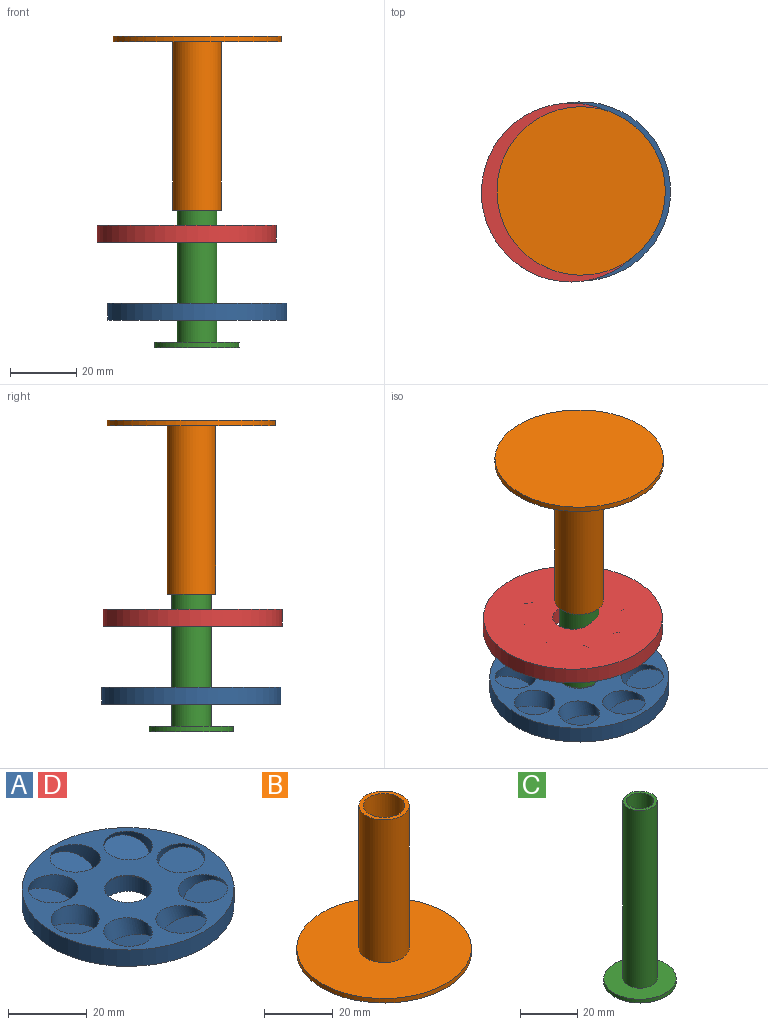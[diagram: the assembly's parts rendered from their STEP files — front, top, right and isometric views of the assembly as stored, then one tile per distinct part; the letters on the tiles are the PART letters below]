
ASSEMBLY  parts=4 mates=2
PART A: 22 faces, bbox 54.9x54.9x9.7 mm
  f0: cylinder r=26.99mm len=53.98mm, axis (0,0,-1), area 861.4mm2, adj f1,f2
  f1: plane 54.89x54.89mm, normal (0,0,1), area 1194.7mm2, adj f0,f4,f6,f8,f9,f11,f13,f15
  f2: plane 53.98x53.98mm, normal (0,0,-1), area 2171.4mm2, adj f0,f19
  f3: plane 12.02x11.79mm, normal (-0.17,0.25,0.95), area 116.7mm2, adj f4
  f4: cylinder r=6.1mm len=13.09mm, axis (-0.17,0.25,0.95), area 121.6mm2, adj f1,f3
  f5: plane 12.02x11.79mm, normal (0.17,-0.25,0.95), area 116.7mm2, adj f6
  f6: cylinder r=6.1mm len=13.09mm, axis (0.17,-0.25,0.95), area 121.4mm2, adj f1,f5
  f7: plane 12.02x11.79mm, normal (-0.25,-0.17,0.95), area 116.7mm2, adj f8
  f8: cylinder r=6.1mm len=13.09mm, axis (-0.25,-0.17,0.95), area 121.6mm2, adj f1,f7
  f9: cylinder r=6.1mm len=13.09mm, axis (0.25,0.17,0.95), area 121.4mm2, adj f1,f10
  f10: plane 12.02x11.79mm, normal (0.25,0.17,0.95), area 116.7mm2, adj f9
  f11: cylinder r=6.1mm len=13.17mm, axis (0.3,-0.06,0.95), area 121.6mm2, adj f1,f12
  f12: plane 12.17x11.64mm, normal (0.3,-0.06,0.95), area 116.7mm2, adj f11
  f13: cylinder r=6.1mm len=13.17mm, axis (-0.3,0.06,0.95), area 119.7mm2, adj f1,f14
  f14: plane 12.17x11.64mm, normal (-0.3,0.06,0.95), area 116.7mm2, adj f13
  f15: cylinder r=6.1mm len=13.17mm, axis (-0.06,-0.3,0.95), area 121.6mm2, adj f1,f16
  f16: plane 12.17x11.64mm, normal (-0.06,-0.3,0.95), area 116.7mm2, adj f15
  f17: cylinder r=6.1mm len=13.17mm, axis (0.06,0.3,0.95), area 119.7mm2, adj f1,f18
  f18: plane 12.17x11.64mm, normal (0.06,0.3,0.95), area 116.7mm2, adj f17
  f19: cylinder r=6.1mm len=12.19mm, axis (0,0,1), area 186.8mm2, adj f2,f20
  f20: plane 12.19x12.19mm, normal (0,0,-1), area 3.9mm2, adj f19,f21
  f21: cylinder r=5.99mm len=11.99mm, axis (0,0,-1), area 7.7mm2, adj f1,f20
PART B: 7 faces, bbox 50.8x50.8x52.4 mm
  f0: cylinder r=25.4mm len=50.8mm, axis (0,0,-1), area 253.4mm2, adj f1,f2
  f1: plane 50.8x50.8mm, normal (0,0,1), area 1859.3mm2, adj f0,f4
  f2: plane 50.8x50.8mm, normal (0,0,-1), area 2026.8mm2, adj f0
  f3: cylinder r=6.03mm len=50.8mm, axis (0,0,-1), area 1925.5mm2, adj f5,f6
  f4: cylinder r=7.3mm len=50.8mm, axis (0,0,-1), area 2330.9mm2, adj f1,f5
  f5: plane 14.61x14.61mm, normal (0,0,1), area 53.2mm2, adj f3,f4
  f6: plane 12.07x12.07mm, normal (0,0,1), area 114.3mm2, adj f3
PART C: 6 faces, bbox 25.4x25.4x77.8 mm
  f0: cylinder r=4.76mm len=77.79mm, axis (0,0,-1), area 2327.7mm2, adj f3,f5
  f1: cylinder r=12.7mm len=25.4mm, axis (0,0,-1), area 126.7mm2, adj f2,f3
  f2: plane 25.4x25.4mm, normal (0,0,1), area 394.8mm2, adj f1,f4
  f3: plane 25.4x25.4mm, normal (0,0,-1), area 435.5mm2, adj f0,f1
  f4: cylinder r=5.97mm len=76.2mm, axis (0,0,-1), area 2857.8mm2, adj f2,f5
  f5: plane 11.94x11.94mm, normal (0,0,1), area 40.7mm2, adj f0,f4
PART D: same geometry as A
PLACE A t=(0,0,-2.44)mm
PLACE B rot(axis=(1,0,0),180deg) t=(0,0,83.16)mm
PLACE C rot(axis=(0,0,1),180deg) t=(0,0,-10.71)mm
PLACE D rot(axis=(0.94,-0.35,0),180deg) t=(-3.08,-0.37,26.17)mm
MATE slider A.f19 <-> C.f4  axis (0,0,-1) through (0,0,-2.44)mm
MATE slider B.f4 <-> C.f4  axis (0,0,1) through (0,0,56.17)mm
